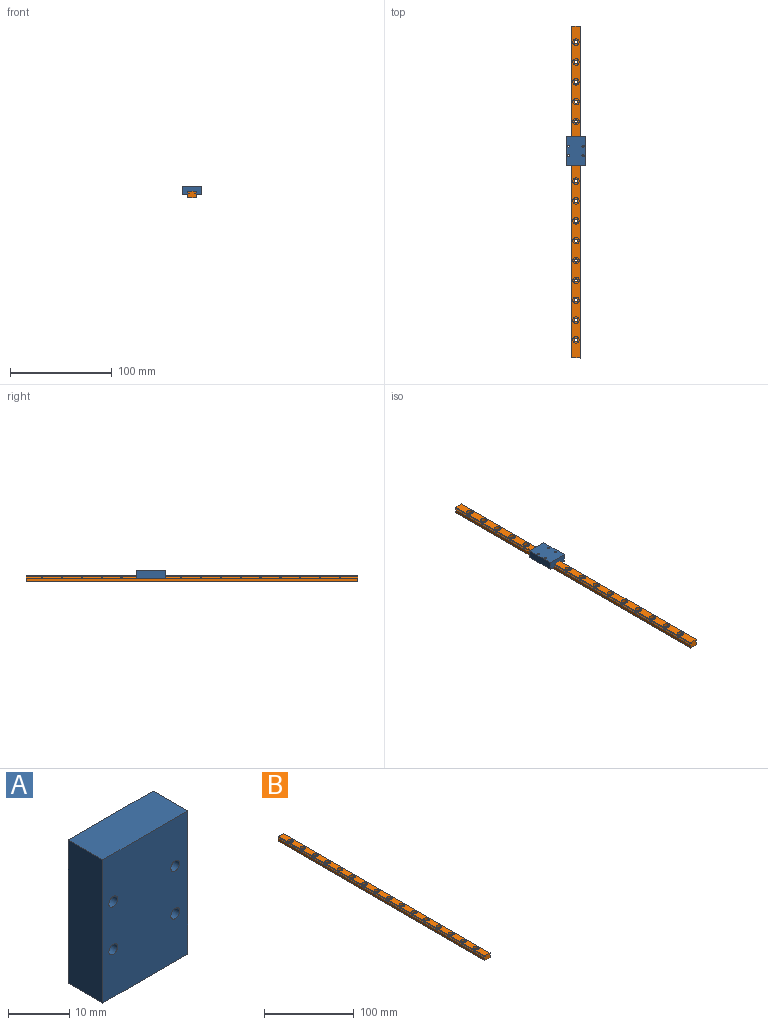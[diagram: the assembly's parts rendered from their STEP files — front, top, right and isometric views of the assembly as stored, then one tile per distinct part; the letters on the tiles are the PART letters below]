
ASSEMBLY  parts=2 mates=1
PART A: 10 faces, bbox 19.6x8x28.6 mm
  f0: plane 19.56x7.95mm, normal (0,0,1), area 155.5mm2, adj f1,f7,f8,f9
  f1: plane 28.58x7.95mm, normal (-1,0,0), area 227.2mm2, adj f0,f2,f8,f9
  f2: plane 19.56x7.95mm, normal (0,0,-1), area 155.5mm2, adj f1,f7,f8,f9
  f3: cylinder r=1.02mm len=7.95mm, axis (0,1,0), area 50.8mm2, adj f8,f9
  f4: cylinder r=1.02mm len=7.95mm, axis (0,1,0), area 50.8mm2, adj f8,f9
  f5: cylinder r=1.02mm len=7.95mm, axis (0,1,0), area 50.8mm2, adj f8,f9
  f6: cylinder r=1.02mm len=7.95mm, axis (0,1,0), area 50.8mm2, adj f8,f9
  f7: plane 28.58x7.95mm, normal (1,0,0), area 227.2mm2, adj f0,f2,f8,f9
  f8: plane 28.58x19.56mm, normal (0,-1,0), area 545.9mm2, adj f0,f1,f2,f3,f4,f5,f6,f7
  f9: plane 28.58x19.56mm, normal (0,1,0), area 545.9mm2, adj f0,f1,f2,f3,f4,f5,f6,f7
PART B: 60 faces, bbox 8x327x6.4 mm
  f0: plane 327.03x3.18mm, normal (-1,0,0), area 1038.3mm2, adj f1,f9,f10,f11
  f1: plane 327.03x7.95mm, normal (0,0,-1), area 2473.2mm2, adj f0,f2,f10,f11,f44,f45,f46,f47
  f2: plane 327.03x3.18mm, normal (1,0,0), area 1038.3mm2, adj f1,f3,f10,f11
  f3: plane 327.03x1.25mm, normal (0.76,0,0.65), area 528.1mm2, adj f2,f4,f10,f11,f12,f14,f16,f18
  f4: plane 327.03x1.07mm, normal (0.65,0,-0.76), area 450.8mm2, adj f3,f5,f10,f11,f12,f14,f16,f18
  f5: plane 327.03x1.02mm, normal (1,0,0), area 332.3mm2, adj f4,f6,f10,f11
  f6: plane 327.03x7.95mm, normal (0,0,1), area 2093.2mm2, adj f5,f7,f10,f11,f12,f14,f16,f18
  f7: plane 327.03x1.02mm, normal (-1,0,0), area 332.3mm2, adj f6,f8,f10,f11
  f8: plane 327.03x1.07mm, normal (-0.65,0,-0.76), area 446.7mm2, adj f7,f9,f10,f11,f12,f14,f16,f18
  f9: plane 327.03x1.25mm, normal (-0.76,0,0.65), area 523.3mm2, adj f0,f8,f10,f11,f12,f14,f16,f18
  f10: plane 7.95x6.35mm, normal (0,-1,0), area 48.2mm2, adj f0,f1,f2,f3,f4,f5,f6,f7
  f11: plane 7.95x6.35mm, normal (0,1,0), area 48.2mm2, adj f0,f1,f2,f3,f4,f5,f6,f7
  f12: cylinder r=3.17mm len=6.35mm, axis (0,0,1), area 61.4mm2, adj f3,f4,f6,f8,f9,f13
  f13: plane 6.35x6.35mm, normal (0,0,1), area 23.8mm2, adj f12,f59
  f14: cylinder r=3.17mm len=6.35mm, axis (0,0,1), area 61.4mm2, adj f3,f4,f6,f8,f9,f15
  f15: plane 6.35x6.35mm, normal (0,0,1), area 23.8mm2, adj f14,f58
  f16: cylinder r=3.17mm len=6.35mm, axis (0,0,1), area 61.4mm2, adj f3,f4,f6,f8,f9,f17
  f17: plane 6.35x6.35mm, normal (0,0,1), area 23.8mm2, adj f16,f57
  f18: cylinder r=3.17mm len=6.35mm, axis (0,0,1), area 61.4mm2, adj f3,f4,f6,f8,f9,f19
  f19: plane 6.35x6.35mm, normal (0,0,1), area 23.8mm2, adj f18,f56
  f20: cylinder r=3.17mm len=6.35mm, axis (0,0,1), area 61.4mm2, adj f3,f4,f6,f8,f9,f21
  f21: plane 6.35x6.35mm, normal (0,0,1), area 23.8mm2, adj f20,f55
  f22: cylinder r=3.17mm len=6.35mm, axis (0,0,1), area 61.4mm2, adj f3,f4,f6,f8,f9,f23
  f23: plane 6.35x6.35mm, normal (0,0,1), area 23.8mm2, adj f22,f54
  f24: cylinder r=3.17mm len=6.35mm, axis (0,0,1), area 61.4mm2, adj f3,f4,f6,f8,f9,f25
  f25: plane 6.35x6.35mm, normal (0,0,1), area 23.8mm2, adj f24,f53
  f26: cylinder r=3.17mm len=6.35mm, axis (0,0,1), area 61.4mm2, adj f3,f4,f6,f8,f9,f27
  f27: plane 6.35x6.35mm, normal (0,0,1), area 23.8mm2, adj f26,f52
  f28: cylinder r=3.17mm len=6.35mm, axis (0,0,1), area 61.4mm2, adj f3,f4,f6,f8,f9,f29
  f29: plane 6.35x6.35mm, normal (0,0,1), area 23.8mm2, adj f28,f51
  f30: cylinder r=3.17mm len=6.35mm, axis (0,0,1), area 61.4mm2, adj f3,f4,f6,f8,f9,f31
  f31: plane 6.35x6.35mm, normal (0,0,1), area 23.8mm2, adj f30,f50
  f32: cylinder r=3.17mm len=6.35mm, axis (0,0,1), area 61.4mm2, adj f3,f4,f6,f8,f9,f33
  f33: plane 6.35x6.35mm, normal (0,0,1), area 23.8mm2, adj f32,f49
  f34: cylinder r=3.17mm len=6.35mm, axis (0,0,1), area 61.4mm2, adj f3,f4,f6,f8,f9,f35
  f35: plane 6.35x6.35mm, normal (0,0,1), area 23.8mm2, adj f34,f48
  f36: cylinder r=3.17mm len=6.35mm, axis (0,0,1), area 61.4mm2, adj f3,f4,f6,f8,f9,f37
  f37: plane 6.35x6.35mm, normal (0,0,1), area 23.8mm2, adj f36,f47
  f38: cylinder r=3.17mm len=6.35mm, axis (0,0,1), area 61.4mm2, adj f3,f4,f6,f8,f9,f39
  f39: plane 6.35x6.35mm, normal (0,0,1), area 23.8mm2, adj f38,f46
  f40: cylinder r=3.17mm len=6.35mm, axis (0,0,1), area 61.4mm2, adj f3,f4,f6,f8,f9,f41
  f41: plane 6.35x6.35mm, normal (0,0,1), area 23.8mm2, adj f40,f45
  f42: cylinder r=3.17mm len=6.35mm, axis (0,0,1), area 61.4mm2, adj f3,f4,f6,f8,f9,f43
  f43: plane 6.35x6.35mm, normal (0,0,1), area 23.8mm2, adj f42,f44
  f44: cylinder r=1.59mm len=3.18mm, axis (0,0,1), area 31.7mm2, adj f1,f43
  f45: cylinder r=1.59mm len=3.18mm, axis (0,0,1), area 31.7mm2, adj f1,f41
  f46: cylinder r=1.59mm len=3.18mm, axis (0,0,1), area 31.7mm2, adj f1,f39
  f47: cylinder r=1.59mm len=3.18mm, axis (0,0,1), area 31.7mm2, adj f1,f37
  f48: cylinder r=1.59mm len=3.18mm, axis (0,0,1), area 31.7mm2, adj f1,f35
  f49: cylinder r=1.59mm len=3.18mm, axis (0,0,1), area 31.7mm2, adj f1,f33
  f50: cylinder r=1.59mm len=3.18mm, axis (0,0,1), area 31.7mm2, adj f1,f31
  f51: cylinder r=1.59mm len=3.18mm, axis (0,0,1), area 31.7mm2, adj f1,f29
  f52: cylinder r=1.59mm len=3.18mm, axis (0,0,1), area 31.7mm2, adj f1,f27
  f53: cylinder r=1.59mm len=3.18mm, axis (0,0,1), area 31.7mm2, adj f1,f25
  f54: cylinder r=1.59mm len=3.18mm, axis (0,0,1), area 31.7mm2, adj f1,f23
  f55: cylinder r=1.59mm len=3.18mm, axis (0,0,1), area 31.7mm2, adj f1,f21
  f56: cylinder r=1.59mm len=3.18mm, axis (0,0,1), area 31.7mm2, adj f1,f19
  f57: cylinder r=1.59mm len=3.18mm, axis (0,0,1), area 31.7mm2, adj f1,f17
  f58: cylinder r=1.59mm len=3.18mm, axis (0,0,1), area 31.7mm2, adj f1,f15
  f59: cylinder r=1.59mm len=3.18mm, axis (0,0,1), area 31.7mm2, adj f1,f13
PLACE A rot(axis=(-1,0,0),90deg) t=(-55.61,-87.76,-62.55)mm
PLACE B rot(axis=(0.13,0.98,-0.12),0deg) t=(-40.85,43.58,-59.37)mm fixed
MATE slider A.f2 <-> B.f11  axis (0,-1,0) through (-66.44,-93.83,-62.55)mm
